# Revit family: Electronics_Desono_Biamp_Two-Way-High-Output-Pendant-Mount-Loudspeaker_DP8
name_source: partatom
category: Communication Devices
units: mm (PartAtom-declared; Revit-internal decimal feet)

## family parameters
Cut with Voids When Loaded = No
Host = Face
Maintain Annotation Orientation = No
OmniClass Number = 23.85.10.11.14.14.14
OmniClass Title = Loudspeakers
Part Type = Normal
Room Calculation Point = No
Round Connector Dimension = Use Diameter
Shared = No

## types (2) — shared parameters
Axial Q / DI = 6.4 / 8, 500 Hz to 6 kHz
Connector Description = Terminal block; Low Impedance 8 ohms, 70/100V operation
Controls = Front-face wattage / low impedance selector switch
Crossover Frequency = 1.3 kHz
Default Elevation = 4' - 0"
Description = Desono™ DP8 Two-Way 8-Inch High Output Pendant Mount Loudspeaker
Diameter = 1' - 1 1/2"
Distortion - 10% Full Power = 2nd Harmonic: 500Hz-1.28%;2kHz-0.45%;8kHz-2.52% 3rd Harmonic: 500Hz-1.24%;2kHz-0.23%;8kHz-0.02%
Driver Protection = Self-resetting solid state circuit breaker
Drivers = LF 1 x 8-inch; HF 1 x 1.25-inch exit compression driver
Enclosure = UL 94V-0 rated ABS plastic, matte finish, paintable
Frequency Response = 80 Hz - 20 kHz (± 5dB)
Height = 1' - 5 1/2"
Input Connection = Two 2-position Euroblock connectors
Loudspeaker Type = Two-way, full-range, coaxial pendant mount loudspeaker, 8 ohm or 70V/100V operation
Manufacturer = Biamp
Max Input Ratings (8 ohm) = 150W continuous, 375W program; 34.6 volts RMS, 69.3 volts momentary peak
Maximum Output = 117 dB SPL / 123 dB SPL (peak 8 ohm)
Minimum Impedance = 5.6 ohms @ 200 Hz
Mounting/Rigging Provisions = Two PHK-15 pendant hang kits (one for main suspension and one as a safety cable), each including 15ft (4.5m) long 2mm (0.77) high tensile galvanized steel wire rope suspension cables with integrated spring clips for attaching the cable to the loudspeaker bracket and Gripple® brand adjustable height cable fasteners
Nominal Coverage = 100º conical (1 kHz to 6 kHz); 115º conical (500 Hz to 6 kHz)
Nominal Impedance = 8 ohms
Operating Range = 60 Hz - 22 kHz
Product Documentation Link = https://downloads.biamp.com
Product Page URL = https://www.biamp.com
Product data url = https://www.bimobject.com
Recommended High Pass Filter = 60 Hz / 24dB octive
Sensitivity (1W/1m) = 95 dB SPL (120 Hz to 12.5 kHz 1/3 octave bands); 94 dB SPL (250 Hz to 4 kHz speech range)
Transformer Taps = 70V:120W, 60W, 30W, 15W and low impedance; 100V:120W, 60W, 30W
URL = https://www.biamp.com
Weight = 16.53 lb

## per-type parameters (varying)
| type | Bracket Material | Grill Material | Housing Material |
| DP8 W | Biamp - Metal - White | Biamp - Plastic - White(Grid) | Biamp - Plastic - White |
| DP8 B | Biamp - Metal - Black | Biamp - Plastic - Black(Grid) | Biamp - Plastic - Black |

note: column(s) folded — value = type name in every type: Model

## geometry (parser evidence)
native form markers: Sweep x2
no freeform markers — native parametric forms only
